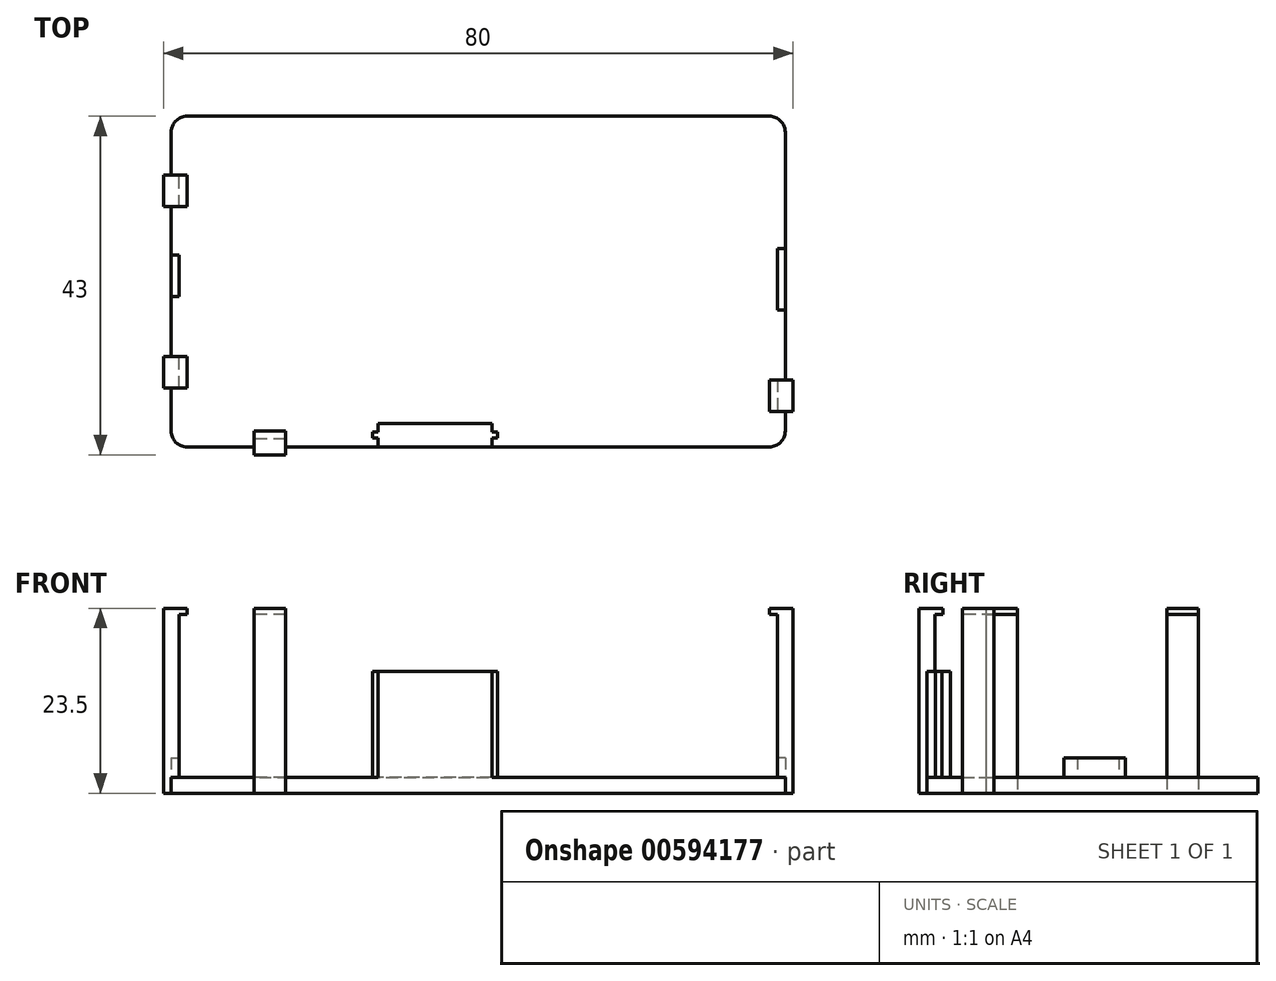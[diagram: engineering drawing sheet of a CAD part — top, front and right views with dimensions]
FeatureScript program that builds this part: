
annotation { "Feature Type Name" : "Feature", "Feature Type Description" : "" }
export const myFeature = defineFeature(function(context is Context, id is Id, definition is map)
    precondition{}
    {
        {
            var Q0;
            Q0=qCreatedBy(makeId("Top.planeOp"),FACE);
            var sketch = newSketch(context, id + "F0", { "sketchPlane" : qUnion([Q0])});
            skLineSegment(sketch, "E0.bottom", {"start": v(0, 0) * mm, "end": v(78, 0) * mm});
            skLineSegment(sketch, "E0.top", {"start": v(0, 42) * mm, "end": v(78, 42) * mm});
            skLineSegment(sketch, "E0.left", {"start": v(0, 0) * mm, "end": v(0, 42) * mm});
            skLineSegment(sketch, "E0.right", {"start": v(78, 0) * mm, "end": v(78, 42) * mm});
            skSolve(sketch);
        }
        {
            var Q0;
            Q0=makeQuery(id+"F0.imprint","IMPRINT",FACE,{"disambiguationData":[TD([[makeQuery(id+"F0.imprint","IMPRINT",EDGE,{"derivedFrom":sQuery(id+"F0.wireOp",EDGE,"E0.bottom")}),1.0]])]});
            extrude(context, id + "F1", {"entities" : qUnion([Q0]), "depth" : 2 * mm, "offsetDistance" : 25 * mm});
        }
        {
            var Q0;
            Q0=makeQuery(id+"F1.opExtrude","CAP_FACE",FACE,{"disambiguationData":[OSD([sQuery(id+"F0.wireOp",EDGE,"E0.bottom"),sQuery(id+"F0.wireOp",EDGE,"E0.top"),sQuery(id+"F0.wireOp",EDGE,"E0.left"),sQuery(id+"F0.wireOp",EDGE,"E0.right")])],"isStart":true});
            var sketch = newSketch(context, id + "F2", { "sketchPlane" : qUnion([Q0])});
            skLineSegment(sketch, "E1.0", {"start": v(0, -42) * mm, "end": v(78, -42) * mm, "construction": true});
            skLineSegment(sketch, "E2.0", {"start": v(0, 0) * mm, "end": v(0, -42) * mm, "construction": true});
            skLineSegment(sketch, "E3.0", {"start": v(0, 0) * mm, "end": v(78, 0) * mm, "construction": true});
            skPoint(sketch, "E4.0", {"position": v(78, -21) * mm});
            skLineSegment(sketch, "E5.0", {"start": v(78, 0) * mm, "end": v(78, -42) * mm, "construction": true});
            skLineSegment(sketch, "E6.bottom", {"start": v(-1, -34.5) * mm, "end": v(1, -34.5) * mm});
            skLineSegment(sketch, "E6.top", {"start": v(-1, -30.5) * mm, "end": v(1, -30.5) * mm});
            skLineSegment(sketch, "E6.left", {"start": v(-1, -34.5) * mm, "end": v(-1, -30.5) * mm});
            skLineSegment(sketch, "E6.right", {"start": v(1, -34.5) * mm, "end": v(1, -30.5) * mm});
            skLineSegment(sketch, "E7.bottom", {"start": v(10.5, -1) * mm, "end": v(14.5, -1) * mm});
            skLineSegment(sketch, "E7.top", {"start": v(10.5, 1) * mm, "end": v(14.5, 1) * mm});
            skLineSegment(sketch, "E7.left", {"start": v(10.5, -1) * mm, "end": v(10.5, 1) * mm});
            skLineSegment(sketch, "E7.right", {"start": v(14.5, -1) * mm, "end": v(14.5, 1) * mm});
            skLineSegment(sketch, "E8.bottom", {"start": v(77, -8.5) * mm, "end": v(79, -8.5) * mm});
            skLineSegment(sketch, "E8.top", {"start": v(77, -4.5) * mm, "end": v(79, -4.5) * mm});
            skLineSegment(sketch, "E8.left", {"start": v(77, -8.5) * mm, "end": v(77, -4.5) * mm});
            skLineSegment(sketch, "E8.right", {"start": v(79, -8.5) * mm, "end": v(79, -4.5) * mm});
            skLineSegment(sketch, "E9.bottom", {"start": v(-1, -11.5) * mm, "end": v(1, -11.5) * mm});
            skLineSegment(sketch, "E9.top", {"start": v(-1, -7.5) * mm, "end": v(1, -7.5) * mm});
            skLineSegment(sketch, "E9.left", {"start": v(-1, -11.5) * mm, "end": v(-1, -7.5) * mm});
            skLineSegment(sketch, "E9.right", {"start": v(1, -11.5) * mm, "end": v(1, -7.5) * mm});
            skSolve(sketch);
        }
        {
            var Q0;
            Q0 = qSketchRegion(id + "F2", true);
            extrude(context, id + "F3", {"entities" : qUnion([Q0]), "operationType" : NewBodyOperationType.ADD, "oppositeDirection" : true, "depth" : 23.5 * mm, "offsetDistance" : 25 * mm});
        }
        {
            var Q0;
            Q0=makeQuery(id+"F1.opExtrude","CAP_FACE",FACE,{"disambiguationData":[OSD([sQuery(id+"F0.wireOp",EDGE,"E0.bottom"),sQuery(id+"F0.wireOp",EDGE,"E0.top"),sQuery(id+"F0.wireOp",EDGE,"E0.left"),sQuery(id+"F0.wireOp",EDGE,"E0.right")])],"isStart":false});
            var sketch = newSketch(context, id + "F4", { "sketchPlane" : qUnion([Q0])});
            skLineSegment(sketch, "E10.0", {"start": v(14.5, 0) * mm, "end": v(78, 0) * mm, "construction": true});
            skLineSegment(sketch, "E11.0", {"start": v(78, 0) * mm, "end": v(78, 4.5) * mm, "construction": true});
            skLineSegment(sketch, "E12.bottom", {"start": v(40.75, 0) * mm, "end": v(26.25, 0) * mm});
            skLineSegment(sketch, "E12.top", {"start": v(40.75, 3) * mm, "end": v(26.25, 3) * mm});
            skLineSegment(sketch, "E12.left", {"start": v(40.75, 0) * mm, "end": v(40.75, 1.1) * mm});
            skLineSegment(sketch, "E12.right", {"start": v(26.25, 0) * mm, "end": v(26.25, 1.1) * mm});
            skLineSegment(sketch, "E13.bottom", {"start": v(40.75, 1.9) * mm, "end": v(41.45, 1.9) * mm});
            skLineSegment(sketch, "E13.top", {"start": v(40.75, 1.1) * mm, "end": v(41.45, 1.1) * mm});
            skLineSegment(sketch, "E13.right", {"start": v(41.45, 1.9) * mm, "end": v(41.45, 1.1) * mm});
            skLineSegment(sketch, "E14.bottom", {"start": v(26.25, 1.9) * mm, "end": v(25.55, 1.9) * mm});
            skLineSegment(sketch, "E14.top", {"start": v(26.25, 1.1) * mm, "end": v(25.55, 1.1) * mm});
            skLineSegment(sketch, "E14.right", {"start": v(25.55, 1.9) * mm, "end": v(25.55, 1.1) * mm});
            skLineSegment(sketch, "E15.trimOffspring", {"start": v(26.25, 1.9) * mm, "end": v(26.25, 3) * mm});
            skLineSegment(sketch, "E16.trimOffspring", {"start": v(40.75, 1.9) * mm, "end": v(40.75, 3) * mm});
            skSolve(sketch);
        }
        {
            var Q0;
            Q0=makeQuery(id+"F4.imprint","IMPRINT",FACE,{"disambiguationData":[TD([[makeQuery(id+"F4.imprint","IMPRINT",EDGE,{"derivedFrom":sQuery(id+"F4.wireOp",EDGE,"E12.bottom")}),1.0]])]});
            extrude(context, id + "F5", {"entities" : qUnion([Q0]), "operationType" : NewBodyOperationType.ADD, "depth" : 13.5 * mm, "offsetDistance" : 25 * mm});
        }
        {
            var Q0;
            Q0=makeQuery(id+"F1.opExtrude","CAP_FACE",FACE,{"disambiguationData":[OSD([sQuery(id+"F0.wireOp",EDGE,"E0.bottom"),sQuery(id+"F0.wireOp",EDGE,"E0.top"),sQuery(id+"F0.wireOp",EDGE,"E0.left"),sQuery(id+"F0.wireOp",EDGE,"E0.right")])],"isStart":false});
            var sketch = newSketch(context, id + "F6", { "sketchPlane" : qUnion([Q0])});
            skPoint(sketch, "E17.0", {"position": v(0, 42) * mm});
            skPoint(sketch, "E18.0", {"position": v(0, 0) * mm});
            skPoint(sketch, "E19.0", {"position": v(78, 42) * mm});
            skPoint(sketch, "E20.0", {"position": v(78, 0) * mm});
            skLineSegment(sketch, "E21.bottom", {"start": v(0, 24.4) * mm, "end": v(1, 24.4) * mm});
            skLineSegment(sketch, "E21.top", {"start": v(0, 19.1) * mm, "end": v(1, 19.1) * mm});
            skLineSegment(sketch, "E21.left", {"start": v(0, 24.4) * mm, "end": v(0, 19.1) * mm});
            skLineSegment(sketch, "E21.right", {"start": v(1, 24.4) * mm, "end": v(1, 19.1) * mm});
            skLineSegment(sketch, "E22.bottom", {"start": v(78, 25.2) * mm, "end": v(77, 25.2) * mm});
            skLineSegment(sketch, "E22.top", {"start": v(78, 17.4) * mm, "end": v(77, 17.4) * mm});
            skLineSegment(sketch, "E22.left", {"start": v(78, 25.2) * mm, "end": v(78, 17.4) * mm});
            skLineSegment(sketch, "E22.right", {"start": v(77, 25.2) * mm, "end": v(77, 17.4) * mm});
            skSolve(sketch);
        }
        {
            var Q0;
            Q0 = qSketchRegion(id + "F6", true);
            extrude(context, id + "F7", {"entities" : qUnion([Q0]), "depth" : 2.5 * mm, "offsetDistance" : 25 * mm});
        }
        {
            var Q0;
            Q0=makeQuery(id+"F1.opExtrude","SWEPT_EDGE",EDGE,{"disambiguationData":[OSD([sQuery(id+"F0.wireOp",EDGE,"E0.top"),sQuery(id+"F0.wireOp",EDGE,"E0.right")])]});
            var Q1;
            Q1=makeQuery(id+"F1.opExtrude","SWEPT_EDGE",EDGE,{"disambiguationData":[OSD([sQuery(id+"F0.wireOp",EDGE,"E0.bottom"),sQuery(id+"F0.wireOp",EDGE,"E0.right")])]});
            var Q2;
            Q2=makeQuery(id+"F1.opExtrude","SWEPT_EDGE",EDGE,{"disambiguationData":[OSD([sQuery(id+"F0.wireOp",EDGE,"E0.top"),sQuery(id+"F0.wireOp",EDGE,"E0.left")])]});
            var Q3;
            Q3=makeQuery(id+"F1.opExtrude","SWEPT_EDGE",EDGE,{"disambiguationData":[OSD([sQuery(id+"F0.wireOp",EDGE,"E0.bottom"),sQuery(id+"F0.wireOp",EDGE,"E0.left")])]});
            fillet(context, id + "F8", {"entities" : qUnion([Q0, Q1, Q2, Q3]), "radius" : 2 * mm, "tangentPropagation" : true, "allowEdgeOverflow" : false});
        }
        {
            var Q0;
            Q0=makeQuery(id+"F3.opExtrude","SWEPT_FACE",FACE,{"disambiguationData":[OSD([sQuery(id+"F2.wireOp",EDGE,"E7.bottom")])]});
            var sketch = newSketch(context, id + "F9", { "sketchPlane" : qUnion([Q0])});
            skLineSegment(sketch, "E23.bottom", {"start": v(-14.5, 23.5) * mm, "end": v(-10.5, 23.5) * mm});
            skLineSegment(sketch, "E23.top", {"start": v(-14.5, 22.7) * mm, "end": v(-10.5, 22.7) * mm});
            skLineSegment(sketch, "E23.left", {"start": v(-14.5, 23.5) * mm, "end": v(-14.5, 22.7) * mm});
            skLineSegment(sketch, "E23.right", {"start": v(-10.5, 23.5) * mm, "end": v(-10.5, 22.7) * mm});
            skSolve(sketch);
        }
        {
            var Q0;
            Q0 = qSketchRegion(id + "F9", true);
            extrude(context, id + "F10", {"entities" : qUnion([Q0]), "operationType" : NewBodyOperationType.ADD, "depth" : 1 * mm, "offsetDistance" : 25 * mm});
        }
        {
            var Q0;
            Q0=makeQuery(id+"F3.opExtrude","SWEPT_FACE",FACE,{"disambiguationData":[OSD([sQuery(id+"F2.wireOp",EDGE,"E8.left")])]});
            var sketch = newSketch(context, id + "F11", { "sketchPlane" : qUnion([Q0])});
            skLineSegment(sketch, "E24.bottom", {"start": v(-8.5, 23.5) * mm, "end": v(-4.5, 23.5) * mm});
            skLineSegment(sketch, "E24.top", {"start": v(-8.5, 22.7) * mm, "end": v(-4.5, 22.7) * mm});
            skLineSegment(sketch, "E24.left", {"start": v(-8.5, 23.5) * mm, "end": v(-8.5, 22.7) * mm});
            skLineSegment(sketch, "E24.right", {"start": v(-4.5, 23.5) * mm, "end": v(-4.5, 22.7) * mm});
            skSolve(sketch);
        }
        {
            var Q0;
            Q0 = qSketchRegion(id + "F11", true);
            extrude(context, id + "F12", {"entities" : qUnion([Q0]), "operationType" : NewBodyOperationType.ADD, "depth" : 1 * mm, "offsetDistance" : 25 * mm});
        }
        {
            var Q0;
            Q0=makeQuery(id+"F3.opExtrude","SWEPT_FACE",FACE,{"disambiguationData":[OSD([sQuery(id+"F2.wireOp",EDGE,"E6.right")])]});
            var sketch = newSketch(context, id + "F13", { "sketchPlane" : qUnion([Q0])});
            skLineSegment(sketch, "E25.bottom", {"start": v(30.5, 23.5) * mm, "end": v(34.5, 23.5) * mm});
            skLineSegment(sketch, "E25.top", {"start": v(30.5, 22.7) * mm, "end": v(34.5, 22.7) * mm});
            skLineSegment(sketch, "E25.left", {"start": v(30.5, 23.5) * mm, "end": v(30.5, 22.7) * mm});
            skLineSegment(sketch, "E25.right", {"start": v(34.5, 23.5) * mm, "end": v(34.5, 22.7) * mm});
            skSolve(sketch);
        }
        {
            var Q0;
            Q0 = qSketchRegion(id + "F13", true);
            extrude(context, id + "F14", {"entities" : qUnion([Q0]), "operationType" : NewBodyOperationType.ADD, "depth" : 1 * mm, "offsetDistance" : 25 * mm});
        }
        {
            var Q0;
            Q0=makeQuery(id+"F3.opExtrude","SWEPT_FACE",FACE,{"disambiguationData":[OSD([sQuery(id+"F2.wireOp",EDGE,"E9.right")])]});
            var sketch = newSketch(context, id + "F15", { "sketchPlane" : qUnion([Q0])});
            skLineSegment(sketch, "E26.bottom", {"start": v(7.5, 23.5) * mm, "end": v(11.5, 23.5) * mm});
            skLineSegment(sketch, "E26.top", {"start": v(7.5, 22.7) * mm, "end": v(11.5, 22.7) * mm});
            skLineSegment(sketch, "E26.left", {"start": v(7.5, 23.5) * mm, "end": v(7.5, 22.7) * mm});
            skLineSegment(sketch, "E26.right", {"start": v(11.5, 23.5) * mm, "end": v(11.5, 22.7) * mm});
            skSolve(sketch);
        }
        {
            var Q0;
            Q0 = qSketchRegion(id + "F15", true);
            extrude(context, id + "F16", {"entities" : qUnion([Q0]), "operationType" : NewBodyOperationType.ADD, "depth" : 1 * mm, "offsetDistance" : 25 * mm});
        }
    });
